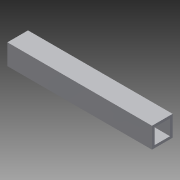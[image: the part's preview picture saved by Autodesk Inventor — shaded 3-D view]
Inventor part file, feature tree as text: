
AUTODESK INVENTOR PART (.ipt)
format: ipt  version: 2014 (Build 180170000, 170)  size: 87,040 bytes
history: native  units: in
note: dims shown in document units (in); Inventor stores cm internally (conversion verified against a paired STEP export)
features: extrude x1, sketch x1
ambient origin geometry x8: Origin, YZ Plane, XZ Plane, XY Plane, X Axis, Y Axis, Z Axis, Center Point
bodies: Solid1 (feature_tree)
feature tree (2):
  extrude  "Extrusion1"  Depth=1.0in
  sketch  "Sketch1"  dims[d0=1.0in d1=1.0in d2=0.125in d3=7.0in d4=0.0in]
